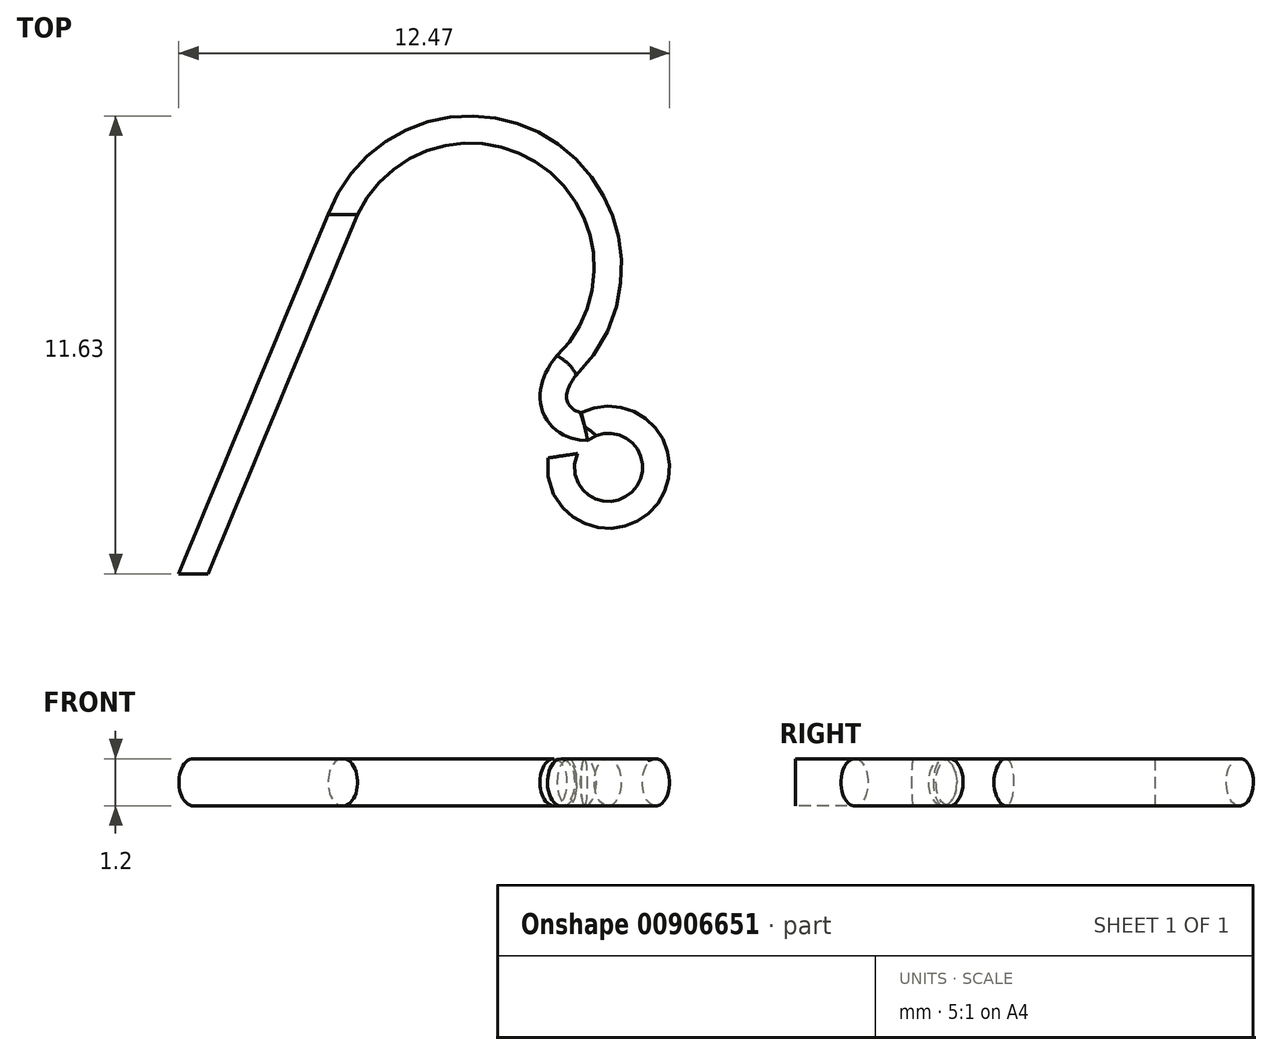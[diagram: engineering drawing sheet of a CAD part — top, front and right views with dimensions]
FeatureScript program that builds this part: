
annotation { "Feature Type Name" : "Feature", "Feature Type Description" : "" }
export const myFeature = defineFeature(function(context is Context, id is Id, definition is map)
    precondition{}
    {
        {
            var Q0;
            Q0=qCreatedBy(makeId("Top.planeOp"),FACE);
            var sketch = newSketch(context, id + "F0", { "sketchPlane" : qUnion([Q0])});
            skArc(sketch, "E0", {"start": v(1.4, 5.33) * mm, "mid": v(0.84, 10.7) * mm, "end": v(-4.32, 9.13) * mm});
            skLineSegment(sketch, "E1", {"start": v(-4.32, 9.13) * mm, "end": v(-8.12, 0) * mm});
            skArc(sketch, "E2", {"start": v(1.82, 3.74) * mm, "mid": v(3.39, 1.98) * mm, "end": v(1.26, 3) * mm});
            skFitSpline(sketch, "E3", {"points": [v(1.4, 5.33) * mm, v(1.82, 3.74) * mm], "startDerivative": vector(-2.08, -2.4) * mm, "endDerivative": vector(2.16, -0.2) * mm});
            skSolve(sketch);
        }
        {
            var Q0;
            Q0=qCreatedBy(makeId("Front.planeOp"),FACE);
            var sketch = newSketch(context, id + "F1", { "sketchPlane" : qUnion([Q0])});
            skEllipse(sketch, "E4", {"center": v(-8.12, 0) * mm, "majorRadius": 0.6 * mm, "minorRadius": 0.38 * mm, "majorAxis": v(0, 1)});
            skSolve(sketch);
        }
        {
            var Q0;
            Q0=makeQuery(id+"F1.imprint","IMPRINT",FACE,{"disambiguationData":[TD([[makeQuery(id+"F1.imprint","IMPRINT",EDGE,{"derivedFrom":sQuery(id+"F1.wireOp",EDGE,"E4")}),1.0]])]});
            var Q1;
            Q1 = qSketchRegion(id + "F0", true);
            var Q2;
            Q2=sQuery(id+"F1.wireOp",EDGE,"E4");
            var Q3;
            Q3=sQuery(id+"F0.wireOp",EDGE,"E1");
            var Q4;
            Q4=sQuery(id+"F0.wireOp",EDGE,"E0");
            var Q5;
            Q5=sQuery(id+"F0.wireOp",EDGE,"E3");
            var Q6;
            Q6=sQuery(id+"F0.wireOp",EDGE,"E2");
            sweep(context, id + "F2", {"profiles" : qUnion([Q0, Q1]), "surfaceProfiles" : qUnion([Q2]), "path" : qUnion([Q3, Q4, Q5, Q6])});
        }
    });
